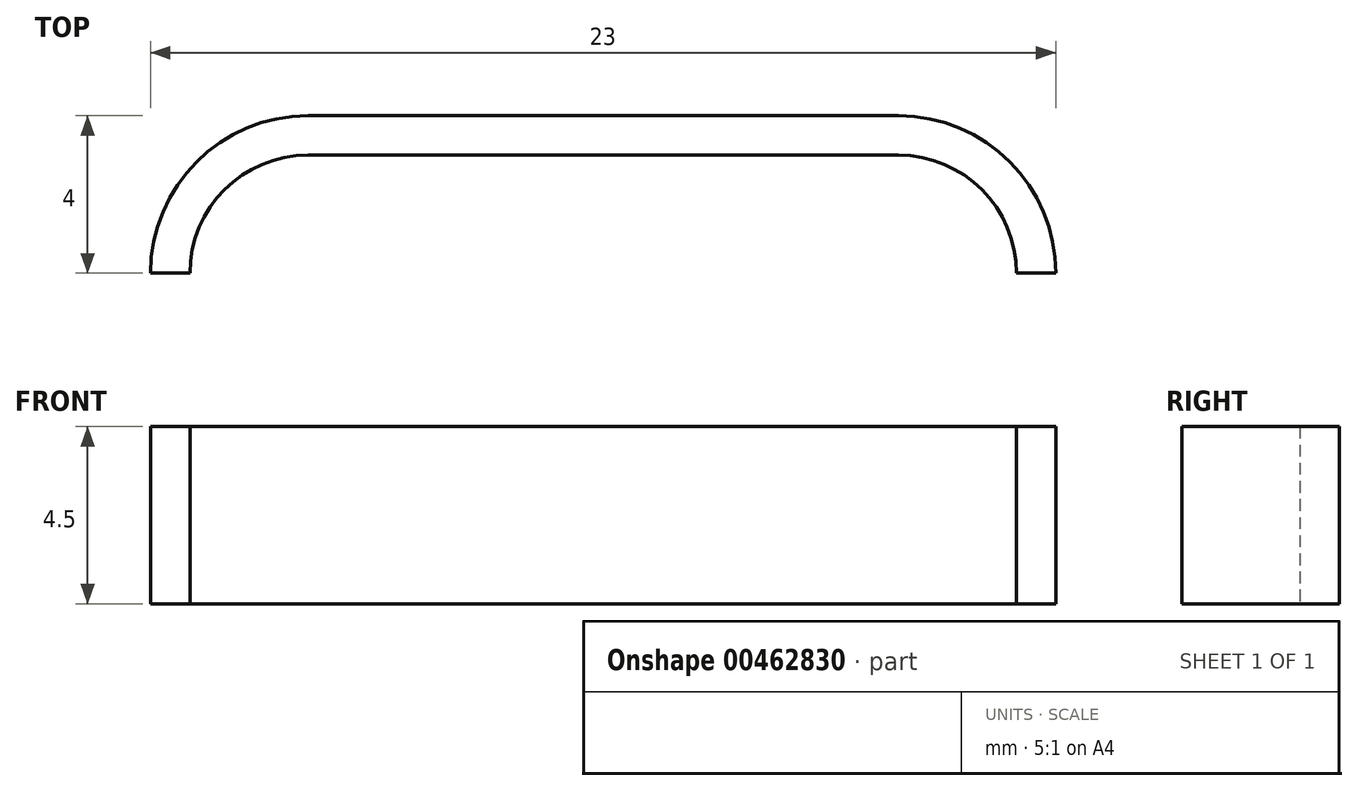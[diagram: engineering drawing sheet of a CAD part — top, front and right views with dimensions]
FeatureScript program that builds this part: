
annotation { "Feature Type Name" : "Feature", "Feature Type Description" : "" }
export const myFeature = defineFeature(function(context is Context, id is Id, definition is map)
    precondition{}
    {
        {
            var Q0;
            Q0=qCreatedBy(makeId("Top.planeOp"),FACE);
            var sketch = newSketch(context, id + "F0", { "sketchPlane" : qUnion([Q0])});
            skLineSegment(sketch, "E0", {"start": v(10.5, 0) * mm, "end": v(10.5, 3) * mm});
            skLineSegment(sketch, "E1", {"start": v(10.5, 3) * mm, "end": v(-10.5, 3) * mm});
            skLineSegment(sketch, "E2", {"start": v(-10.5, 3) * mm, "end": v(-10.5, 0) * mm});
            skLineSegment(sketch, "E3", {"start": v(-10.5, 0) * mm, "end": v(-11.5, 0) * mm});
            skLineSegment(sketch, "E4", {"start": v(-11.5, 0) * mm, "end": v(-11.5, 4) * mm});
            skLineSegment(sketch, "E5", {"start": v(-11.5, 4) * mm, "end": v(11.5, 4) * mm});
            skLineSegment(sketch, "E6", {"start": v(11.5, 4) * mm, "end": v(11.5, 0) * mm});
            skLineSegment(sketch, "E7", {"start": v(11.5, 0) * mm, "end": v(10.5, 0) * mm});
            skSolve(sketch);
        }
        {
            var Q0;
            Q0 = qSketchRegion(id + "F0", true);
            extrude(context, id + "F1", {"entities" : qUnion([Q0]), "depth" : 4.5 * mm});
        }
        {
            var Q0;
            Q0=makeQuery(id+"F1.opExtrude","SWEPT_EDGE",EDGE,{"disambiguationData":[OSD([sQuery(id+"F0.wireOp",EDGE,"E0"),sQuery(id+"F0.wireOp",EDGE,"E1")])]});
            var Q1;
            Q1=makeQuery(id+"F1.opExtrude","SWEPT_EDGE",EDGE,{"disambiguationData":[OSD([sQuery(id+"F0.wireOp",EDGE,"E1"),sQuery(id+"F0.wireOp",EDGE,"E2")])]});
            fillet(context, id + "F2", {"entities" : qUnion([Q0, Q1]), "radius" : 3 * mm, "tangentPropagation" : true, "allowEdgeOverflow" : false});
        }
        {
            var Q0;
            Q0=makeQuery(id+"F1.opExtrude","SWEPT_EDGE",EDGE,{"disambiguationData":[OSD([sQuery(id+"F0.wireOp",EDGE,"E4"),sQuery(id+"F0.wireOp",EDGE,"E5")])]});
            var Q1;
            Q1=makeQuery(id+"F1.opExtrude","SWEPT_EDGE",EDGE,{"disambiguationData":[OSD([sQuery(id+"F0.wireOp",EDGE,"E5"),sQuery(id+"F0.wireOp",EDGE,"E6")])]});
            fillet(context, id + "F3", {"entities" : qUnion([Q0, Q1]), "radius" : 4 * mm, "tangentPropagation" : true, "allowEdgeOverflow" : false});
        }
    });
